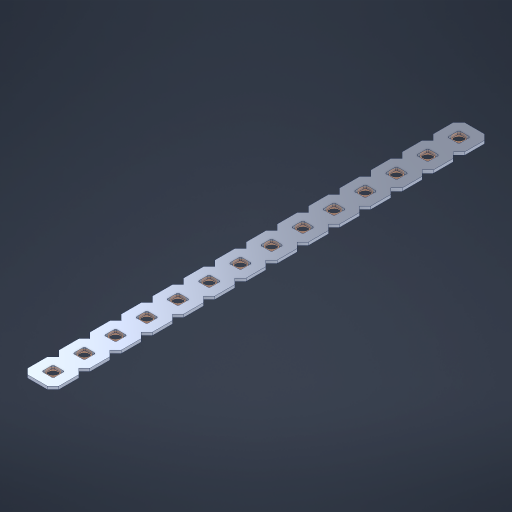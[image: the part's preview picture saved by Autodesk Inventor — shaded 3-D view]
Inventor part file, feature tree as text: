
AUTODESK INVENTOR PART (.ipt)
format: ipt  version: 2023 (Build 270158000, 158)  size: 441,856 bytes
history: native  units: in
note: dims shown in document units (in); Inventor stores cm internally (conversion verified against a paired STEP export)
features: other x15, extrude x13, sketch x2, pattern_linear x1
ambient origin geometry x8: Origin, YZ Plane, XZ Plane, XY Plane, X Axis, Y Axis, Z Axis, Center Point
bodies: Solid1 (feature_tree), Body (feature_tree)
feature tree (31):
  pattern_linear  "Rectangular Pattern1"  Spacing1=0.09in  [1 undecoded]
  sketch  "Sketch1"  dims[d1=0.5in]
  sketch  "Sketch2"  dims[d2=0.182in d3=0.09in d4=0.09in d5=0.09in d6=0.09in d7=0.09in d8=0.09in d9=0.09in d10=0.09in d11=0.02in d13=0.0in d14=0.172in d15=0.0625in d16=0.0in d19=0.5in d22=0.5in]
  other  "Srf1"
  other  "Srf126"
  other  "Srf127"
  other  "Srf128"
  other  "Srf129"
  other  "Srf130"
  other  "Srf131"
  other  "Srf250"
  other  "Srf251"
  other  "Srf252"
  other  "Srf253"
  other  "Srf254"
  other  "Srf255"
  other  "Srf256"
  other  "Circle"
  extrude  "ExtrusionSrf126"  Depth=0.09in
  extrude  "ExtrusionSrf127"  Depth=0.09in
  extrude  "ExtrusionSrf128"  Depth=0.09in
  extrude  "ExtrusionSrf129"  Depth=0.09in
  extrude  "ExtrusionSrf130"  Depth=0.09in
  extrude  "ExtrusionSrf131"  Depth=0.09in
  extrude  "ExtrusionSrf250"  Depth=0.09in
  extrude  "ExtrusionSrf251"  Depth=0.02in
  extrude  "ExtrusionSrf252"  TaperAngle=0.0deg  [1 undecoded]
  extrude  "ExtrusionSrf253"  Depth=0.5in
  extrude  "ExtrusionSrf254"  Depth=0.5in TaperAngle=0.0deg
  extrude  "ExtrusionSrf255"  Depth=0.5in
  extrude  "ExtrusionSrf256"  Depth=0.5in
note: 2 required parameter values undecoded (feature->parameter linkage not recoverable at this tier; creation-order binding heuristic only, values carry confidence <= 0.55)
